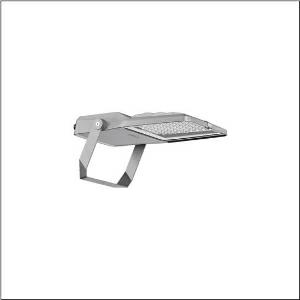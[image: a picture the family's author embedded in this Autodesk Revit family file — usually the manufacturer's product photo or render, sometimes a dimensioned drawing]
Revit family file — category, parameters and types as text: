
# Revit family: floodlight_fl_21_iq_mini___pl52_5xa7772b4d1a_9164
name_source: partatom
category: Lighting Fixtures
units: mm (PartAtom-declared; Revit-internal decimal feet)

## family parameters
Cut with Voids When Loaded = No
Host = Face
Light Source = No
Part Type = Normal
Room Calculation Point = No
Round Connector Dimension = Use Diameter
Shared = No

## types (1)
- --- (1 x LED, 6490 lm, 45.5 W, 4000K)
    Apparent Load = 46 VA
    CIE Flux Codes = 26 60 98 100 100
    Color Rendering = 70
    Color Temperature = 4000K
    Default Elevation = 1800 mm
    Description = Floodlight FL 21 iQ mini, floodlight, primary light control with lens, of PMMA, primary optical cover: protective disc, of toughened safety glass, transparent, light distribution: PL52, light emission: direct distribution, installation type: surface-mounted, lamps: LED, High Power LED, rated values: 6.490lm | 45,5W | 142,6lm/W (begin service life); end service life: 6.490lm | 48W; at 50% lumin. flux: 3.245lm | 21,5W | 150,9lm/W, colour temperature: 4000K, colour rendering: CRI > 70, light colour: 740, light setting 1 begin service life: 100% | 6.490lm | 45,5W | 142,6lm/W | 4.000K, light setting 1 end service life: 48W, further light settings possible, control: Street-Remote, Auto-Match, Temp-Guard, Night-Set, Smart-Wire, Desk-Remote (wireless, voltage-free reading and setting of iQ features in the workshop via application-optimized NFC function/RFID function), optimised constant luminous flux control (CLO 2.0), pre-setting: linear dimming characteristic, with terminal, 6-pole, mains connection: 220..240V, AC, 50/60Hz, luminaire housing, of diecast aluminium, powder-coated, SITECO metallic grey (DB 702S), corrosivity category C5 mid according to DIN EN ISO 12944suitable for swimming poolschlorine-resistant, sealing non-destructively replaceable, mounting bracket, of steel, galvanised, powder-coated, SITECO metallic grey (DB 702S), protection rating (complete): IP66, insulation class (complete): insulation class II (safety insulation), certification: CE, ENEC, VDE, protection symbol: D, impact resistance: IK08, permissible operating ambient temperature: -40..+40°C, permissible operating ambient temperature for outdoor applications: -40..+50°C, standard: DIN EN 12944, LABS conformity tested according to VDMA 24364:2018-05, packaging unit: 1 piece

Light Distribution: PL52
    Height = 70 mm
    Lamp = 1 x LED
    Lamp Light Flux = 6490 lm
    Lamp Power = 45.5 W
    Lamp count = 1
    Length = 485 mm
    Luminous efficacy = 143 lm/W
    Manufacturer = Siteco
    ModVariant = No
    Model = 5XA7772B4D1A
    Number of Poles = 1
    OnlyDefault = Yes
    Power Factor = 1
    Product Name = Floodlight FL 21 iQ mini | PL52
    Product group = floodlight | pylon annexe
    ProductGroupID = 6201
    Protection Class = Protection class II
    Protection Degree = IP 66
    RLX_Detail_Level = 1
    RLX_Emergency_Light_Flux = 0 lm
    RLX_Emergency_Type = 0
    RLX_Emergency_Type_DB = No
    RlxData = <blob elided: 96653 chars, md5=14868645>
    Socket = socket
    Standby Power = 0 W
    System Light Flux = 6490 lm
    System Power = 46 W
    Type Comments = factory setting: luminous flux: 100 % | dim-lin: 254 | 463 mA
    Type Image = l_1006845.jpg
    URL = http://relux.com
    VarID = @adj_164241
    Voltage = 0 V
    Weight = 0.00 kg
    Width = 337 mm

## geometry (parser evidence)
native form markers: Blend x4, Sweep x13
no freeform markers — native parametric forms only
